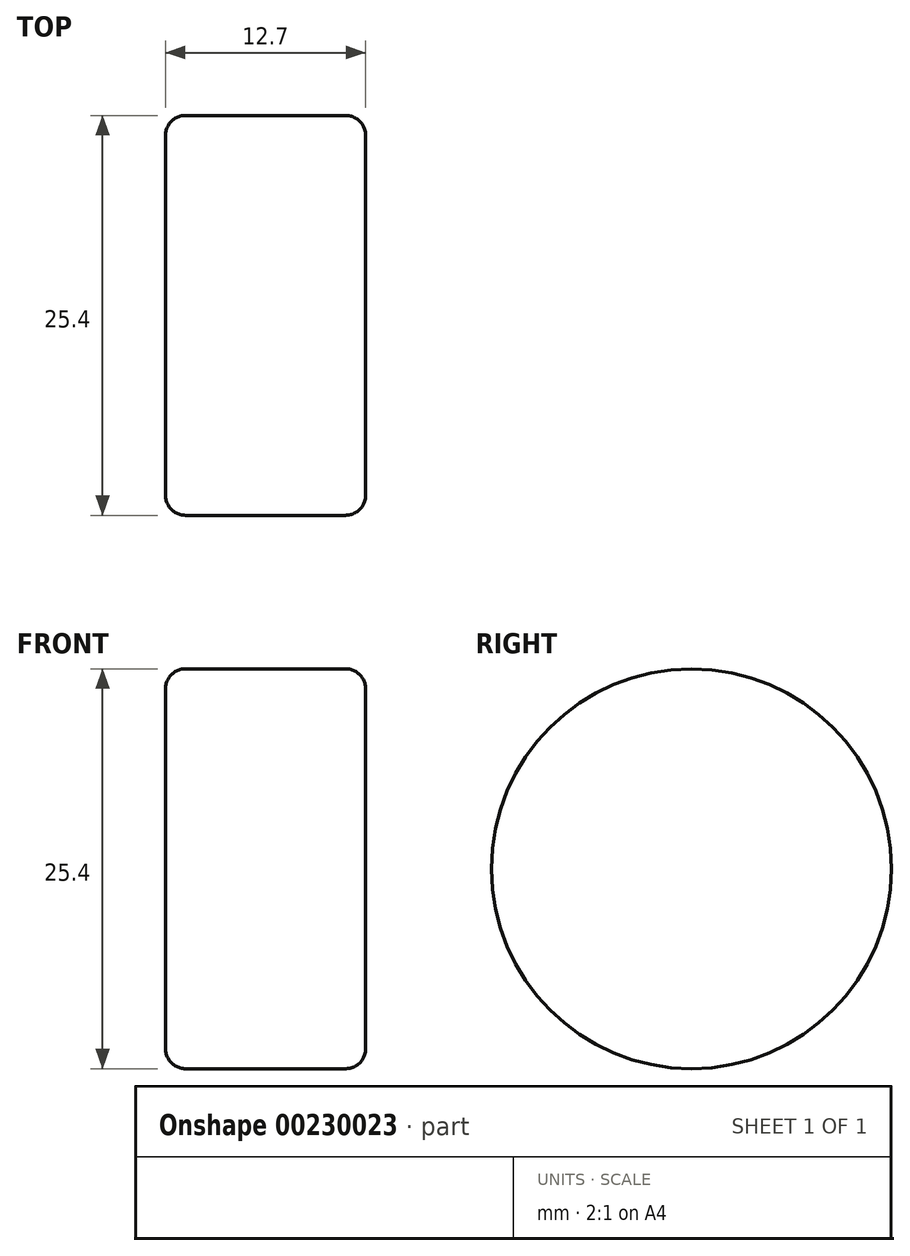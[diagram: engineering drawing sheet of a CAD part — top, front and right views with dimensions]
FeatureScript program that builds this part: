
annotation { "Feature Type Name" : "Feature", "Feature Type Description" : "" }
export const myFeature = defineFeature(function(context is Context, id is Id, definition is map)
    precondition{}
    {
        {
            var Q0;
            Q0=qCreatedBy(makeId("Front.planeOp"),FACE);
            var sketch = newSketch(context, id + "F0", { "sketchPlane" : qUnion([Q0])});
            skLineSegment(sketch, "E0", {"start": v(-18.8, 0) * mm, "end": v(28.89, 0) * mm, "construction": true});
            skLineSegment(sketch, "E1.bottom", {"start": v(-6.35, 0) * mm, "end": v(6.35, 0) * mm});
            skLineSegment(sketch, "E1.top", {"start": v(-5.08, 12.7) * mm, "end": v(5.08, 12.7) * mm});
            skLineSegment(sketch, "E1.left", {"start": v(-6.35, 0) * mm, "end": v(-6.35, 11.43) * mm});
            skLineSegment(sketch, "E1.right", {"start": v(6.35, 0) * mm, "end": v(6.35, 11.43) * mm});
            skPoint(sketch, "E2", {"position": v(0, 12.7) * mm});
            skPoint(sketch, "E3.visualSharp", {"position": v(6.35, 12.7) * mm});
            skArc(sketch, "E3.filletArc", {"start": v(6.35, 11.43) * mm, "mid": v(5.98, 12.33) * mm, "end": v(5.08, 12.7) * mm});
            skPoint(sketch, "E4.visualSharp", {"position": v(-6.35, 12.7) * mm});
            skArc(sketch, "E4.filletArc", {"start": v(-5.08, 12.7) * mm, "mid": v(-5.98, 12.33) * mm, "end": v(-6.35, 11.43) * mm});
            skPoint(sketch, "E5.visualSharp", {"position": v(-6.35, 0) * mm});
            skPoint(sketch, "E6.visualSharp", {"position": v(6.35, 0) * mm});
            skSolve(sketch);
        }
        {
            var Q0;
            Q0 = qSketchRegion(id + "F0", true);
            var Q1;
            Q1=sQuery(id+"F0.wireOp",EDGE,"E0");
            revolve(context, id + "F1", {"entities" : qUnion([Q0]), "axis" : qUnion([Q1]), "revolveType" : RevolveType.FULL});
        }
    });
